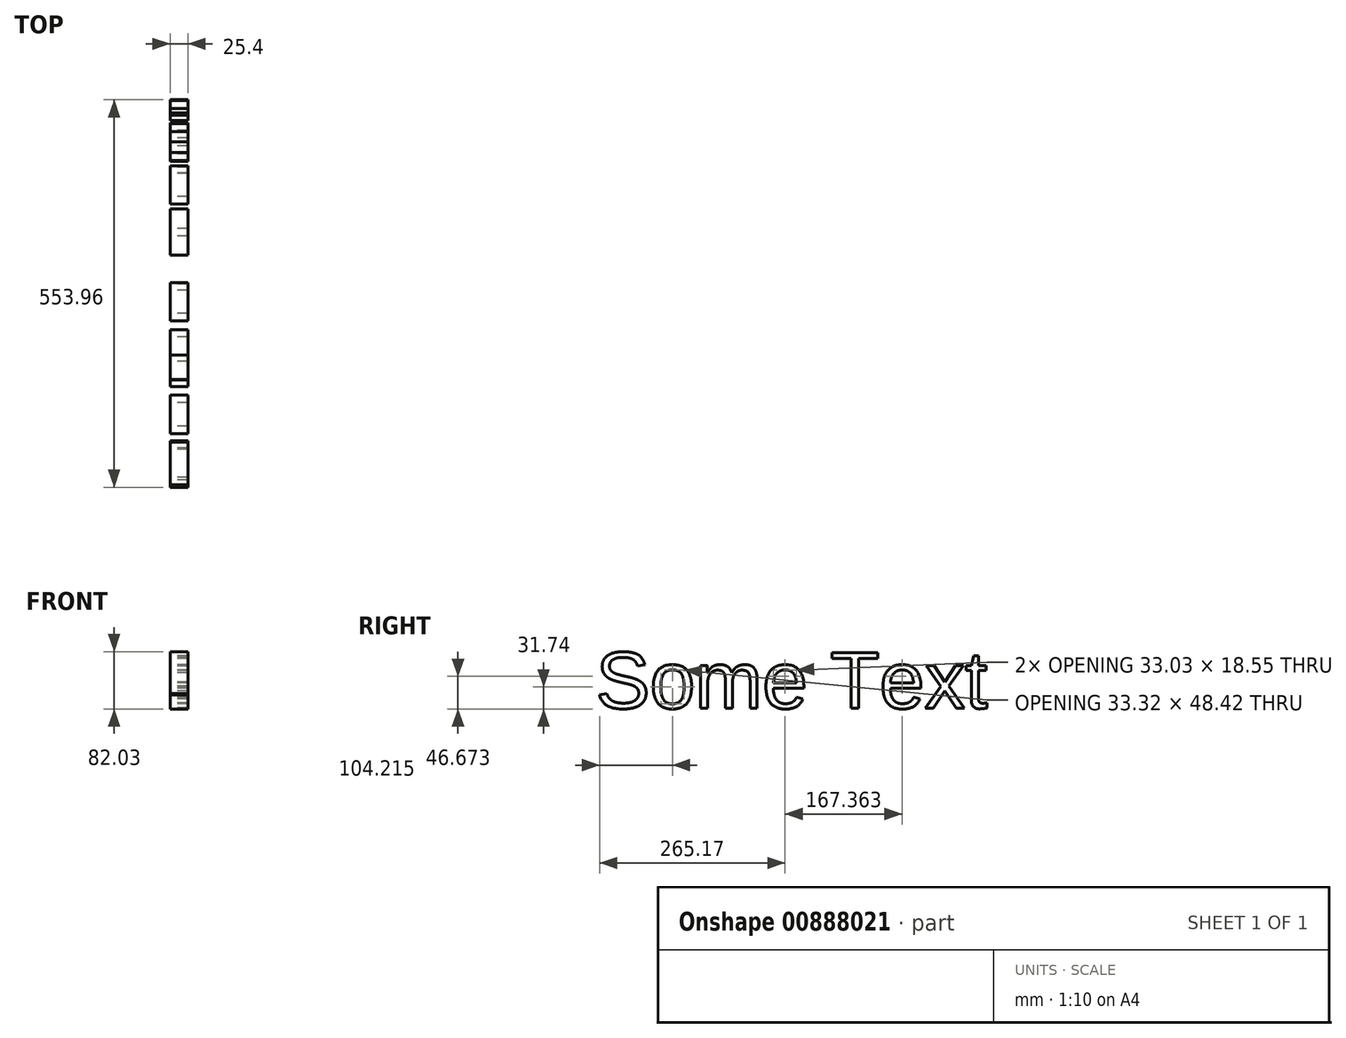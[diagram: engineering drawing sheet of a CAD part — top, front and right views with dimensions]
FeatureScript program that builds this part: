
annotation { "Feature Type Name" : "Feature", "Feature Type Description" : "" }
export const myFeature = defineFeature(function(context is Context, id is Id, definition is map)
    precondition{}
    {
        {
            var Q0;
            Q0=qCreatedBy(makeId("Right.planeOp"),FACE);
            var sketch = newSketch(context, id + "F0", { "sketchPlane" : qUnion([Q0])});
            skText(sketch, "E0", { "text": "Some Text", "fontName": "Arimo-Regular.ttf"});
            const initialGuessF0  = {"E0": [-0.56728, 0, 1, 0, 0.08341]};
            skSetInitialGuess(sketch, initialGuessF0);
            skSolve(sketch);
        }
        {
            var Q0;
            Q0=makeQuery(id+"F0.imprint","IMPRINT",FACE,{"disambiguationData":[TD([[makeQuery(id+"F0.imprint","IMPRINT",EDGE,{"derivedFrom":sQuery(id+"F0.wireOp",EDGE,"E0.sketch_text.stroke-0")}),-1.0]])]});
            var Q1;
            Q1=makeQuery(id+"F0.imprint","IMPRINT",FACE,{"disambiguationData":[TD([[makeQuery(id+"F0.imprint","IMPRINT",EDGE,{"derivedFrom":sQuery(id+"F0.wireOp",EDGE,"E0.sketch_text.stroke-34")}),-1.0]])]});
            var Q2;
            Q2=makeQuery(id+"F0.imprint","IMPRINT",FACE,{"disambiguationData":[TD([[makeQuery(id+"F0.imprint","IMPRINT",EDGE,{"derivedFrom":sQuery(id+"F0.wireOp",EDGE,"E0.sketch_text.stroke-49")}),-1.0]])]});
            var Q3;
            Q3=makeQuery(id+"F0.imprint","IMPRINT",FACE,{"disambiguationData":[TD([[makeQuery(id+"F0.imprint","IMPRINT",EDGE,{"derivedFrom":sQuery(id+"F0.wireOp",EDGE,"E0.sketch_text.stroke-81")}),-1.0]])]});
            var Q4;
            Q4=makeQuery(id+"F0.imprint","IMPRINT",FACE,{"disambiguationData":[TD([[makeQuery(id+"F0.imprint","IMPRINT",EDGE,{"derivedFrom":sQuery(id+"F0.wireOp",EDGE,"E0.sketch_text.stroke-99")}),-1.0]])]});
            var Q5;
            Q5=makeQuery(id+"F0.imprint","IMPRINT",FACE,{"disambiguationData":[TD([[makeQuery(id+"F0.imprint","IMPRINT",EDGE,{"derivedFrom":sQuery(id+"F0.wireOp",EDGE,"E0.sketch_text.stroke-107")}),-1.0]])]});
            var Q6;
            Q6=makeQuery(id+"F0.imprint","IMPRINT",FACE,{"disambiguationData":[TD([[makeQuery(id+"F0.imprint","IMPRINT",EDGE,{"derivedFrom":sQuery(id+"F0.wireOp",EDGE,"E0.sketch_text.stroke-125")}),-1.0]])]});
            var Q7;
            Q7=makeQuery(id+"F0.imprint","IMPRINT",FACE,{"disambiguationData":[TD([[makeQuery(id+"F0.imprint","IMPRINT",EDGE,{"derivedFrom":sQuery(id+"F0.wireOp",EDGE,"E0.sketch_text.stroke-137")}),-1.0]])]});
            extrude(context, id + "F1", {"entities" : qUnion([Q0, Q1, Q2, Q3, Q4, Q5, Q6, Q7]), "depth" : 25.4 * mm, "offsetDistance" : 25.4 * mm});
        }
    });
